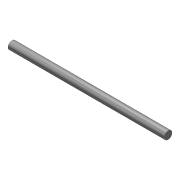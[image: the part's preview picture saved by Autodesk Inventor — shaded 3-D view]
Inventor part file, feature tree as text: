
AUTODESK INVENTOR PART (.ipt)
format: ipt  version: 2016 (Build 200138000, 138)  size: 68,096 bytes
history: native  units: in
note: dims shown in document units (in); Inventor stores cm internally (conversion verified against a paired STEP export)
features: extrude x1, sketch x1
ambient origin geometry x8: Origin, YZ Plane, XZ Plane, XY Plane, X Axis, Y Axis, Z Axis, Center Point
bodies: Solid1 (feature_tree)
feature tree (2):
  extrude  "Extrusion1"  Depth=8.5in TaperAngle=0.0deg
  sketch  "Sketch1"  dims[d0=0.4375in d1=8.5in d2=0.0in]
